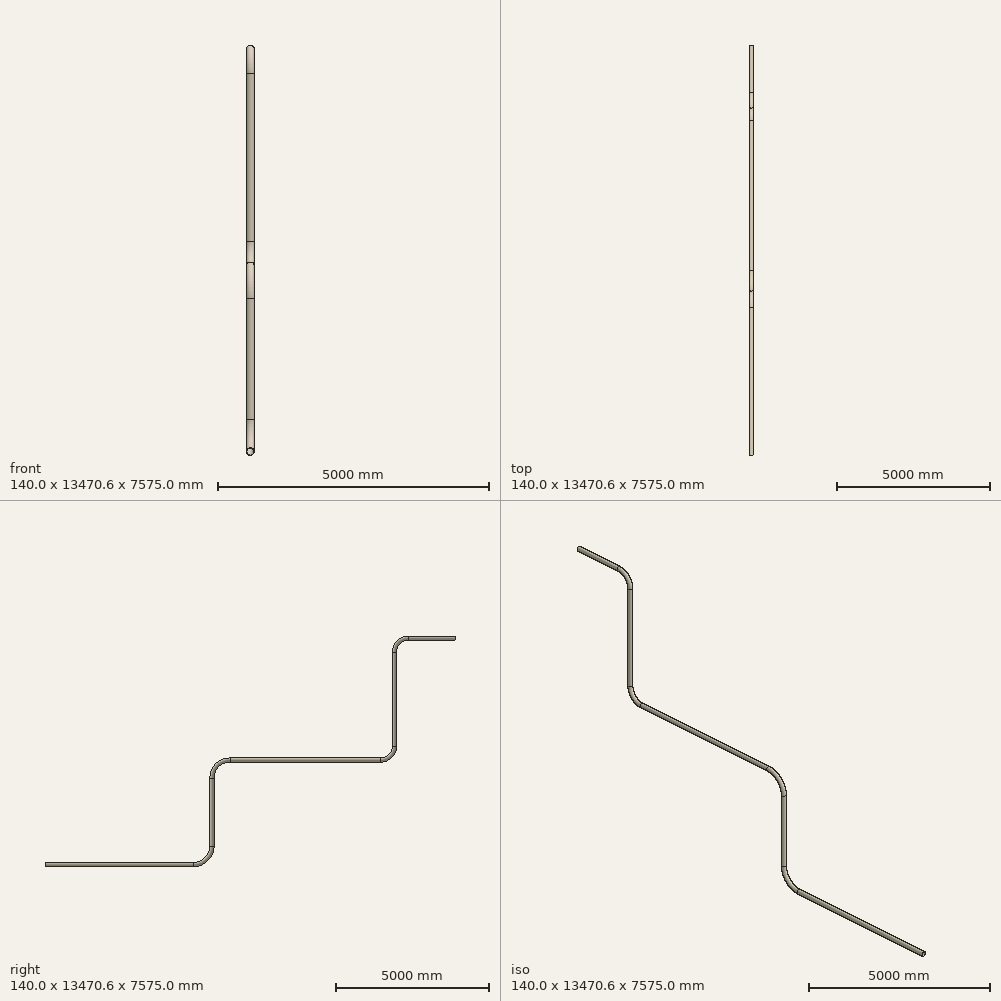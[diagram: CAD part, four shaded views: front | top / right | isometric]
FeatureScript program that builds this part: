
annotation { "Feature Type Name" : "Feature", "Feature Type Description" : "" }
export const myFeature = defineFeature(function(context is Context, id is Id, definition is map)
    precondition{}
    {
        {
            var Q0;
            Q0=qCreatedBy(makeId("Right.planeOp"),FACE);
            var sketch = newSketch(context, id + "F0", { "sketchPlane" : qUnion([Q0])});
            skLineSegment(sketch, "E0", {"start": v(0, 0) * mm, "end": v(-1550, 0) * mm});
            skLineSegment(sketch, "E1", {"start": v(-2000, -450) * mm, "end": v(-2000, -3550) * mm});
            skLineSegment(sketch, "E2", {"start": v(-2450, -4000) * mm, "end": v(-7400, -4000) * mm});
            skPoint(sketch, "E3.visualSharp", {"position": v(-2000, 0) * mm});
            skArc(sketch, "E3.filletArc", {"start": v(-1550, 0) * mm, "mid": v(-1868.2, -131.8) * mm, "end": v(-2000, -450) * mm});
            skPoint(sketch, "E4.visualSharp", {"position": v(-2000, -4000) * mm});
            skArc(sketch, "E4.filletArc", {"start": v(-2450, -4000) * mm, "mid": v(-2131.8, -3868.2) * mm, "end": v(-2000, -3550) * mm});
            skLineSegment(sketch, "E5", {"start": v(-8000, -4600) * mm, "end": v(-8000, -6834.97) * mm});
            skLineSegment(sketch, "E6", {"start": v(-8600, -7434.97) * mm, "end": v(-13470.6, -7434.97) * mm});
            skPoint(sketch, "E7.visualSharp", {"position": v(-8000, -4000) * mm});
            skArc(sketch, "E7.filletArc", {"start": v(-7400, -4000) * mm, "mid": v(-7824.26, -4175.74) * mm, "end": v(-8000, -4600) * mm});
            skPoint(sketch, "E8.visualSharp", {"position": v(-8000, -7434.97) * mm});
            skArc(sketch, "E8.filletArc", {"start": v(-8600, -7434.97) * mm, "mid": v(-8175.74, -7259.24) * mm, "end": v(-8000, -6834.97) * mm});
            skSolve(sketch);
        }
        {
            var Q0;
            Q0=qCreatedBy(makeId("Front.planeOp"),FACE);
            var sketch = newSketch(context, id + "F1", { "sketchPlane" : qUnion([Q0])});
            skCircle(sketch, "E9", {"center": v(0, 0) * mm, "radius": 70 * mm});
            skCircle(sketch, "E10", {"center": v(0, 0) * mm, "radius": 65 * mm});
            skSolve(sketch);
        }
        {
            var Q0;
            Q0=makeQuery(id+"F1.imprint","IMPRINT",FACE,{"disambiguationData":[TD([[makeQuery(id+"F1.imprint","IMPRINT",EDGE,{"derivedFrom":sQuery(id+"F1.wireOp",EDGE,"E9")}),1.0]])]});
            var Q1;
            Q1=sQuery(id+"F0.wireOp",EDGE,"E0");
            var Q2;
            Q2=sQuery(id+"F0.wireOp",EDGE,"E3.filletArc");
            var Q3;
            Q3=sQuery(id+"F0.wireOp",EDGE,"E1");
            var Q4;
            Q4=sQuery(id+"F0.wireOp",EDGE,"E4.filletArc");
            var Q5;
            Q5=sQuery(id+"F0.wireOp",EDGE,"E2");
            var Q6;
            Q6=sQuery(id+"F0.wireOp",EDGE,"E7.filletArc");
            var Q7;
            Q7=sQuery(id+"F0.wireOp",EDGE,"E5");
            var Q8;
            Q8=sQuery(id+"F0.wireOp",EDGE,"E8.filletArc");
            var Q9;
            Q9=sQuery(id+"F0.wireOp",EDGE,"E6");
            sweep(context, id + "F2", {"profiles" : qUnion([Q0]), "path" : qUnion([Q1, Q2, Q3, Q4, Q5, Q6, Q7, Q8, Q9])});
        }
    });
